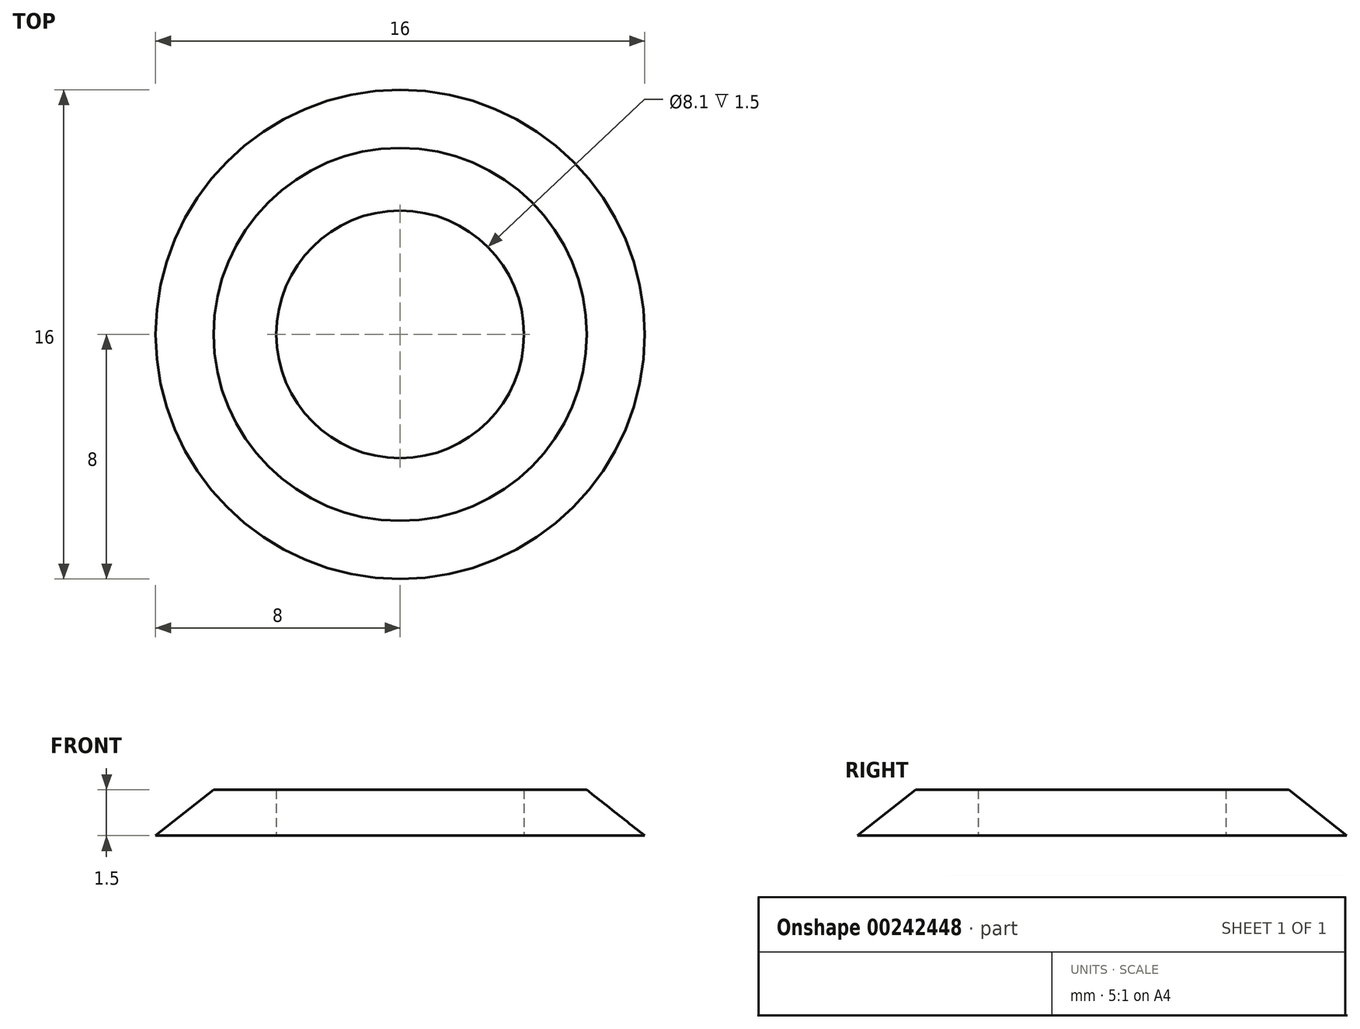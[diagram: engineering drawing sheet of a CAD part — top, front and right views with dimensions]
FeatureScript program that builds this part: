
annotation { "Feature Type Name" : "Feature", "Feature Type Description" : "" }
export const myFeature = defineFeature(function(context is Context, id is Id, definition is map)
    precondition{}
    {
        {
            var Q0;
            Q0=qCreatedBy(makeId("Top.planeOp"),FACE);
            var sketch = newSketch(context, id + "F0", { "sketchPlane" : qUnion([Q0])});
            skCircle(sketch, "E0", {"center": v(0, 0) * mm, "radius": 4.05 * mm});
            skCircle(sketch, "E1", {"center": v(0, 0) * mm, "radius": 6.05 * mm});
            skCircle(sketch, "E2", {"center": v(0, 0) * mm, "radius": 8 * mm});
            skSolve(sketch);
        }
        {
            var Q0;
            Q0=makeQuery(id+"F0.imprint","IMPRINT",FACE,{"disambiguationData":[TD([[makeQuery(id+"F0.imprint","IMPRINT",EDGE,{"derivedFrom":sQuery(id+"F0.wireOp",EDGE,"E0")}),-1.0]])]});
            var Q1;
            Q1=makeQuery(id+"F0.imprint","IMPRINT",FACE,{"disambiguationData":[TD([[makeQuery(id+"F0.imprint","IMPRINT",EDGE,{"derivedFrom":sQuery(id+"F0.wireOp",EDGE,"E1")}),-1.0]])]});
            extrude(context, id + "F1", {"entities" : qUnion([Q0, Q1]), "depth" : 1.5 * mm});
        }
        {
            var Q0;
            Q0=makeQuery(id+"F1.opExtrude","CAP_EDGE",EDGE,{"disambiguationData":[OSD([sQuery(id+"F0.wireOp",EDGE,"E2")])],"isStart":false});
            chamfer(context, id + "F2", {"entities" : qUnion([Q0]), "chamferType" : ChamferType.TWO_OFFSETS, "width1" : 1.9 * mm, "oppositeDirection" : false, "width2" : 1.5 * mm, "tangentPropagation" : true});
        }
    });
